# Revit family: Domotics-DomesticRanges-GEWISS-CHORUS_COMMAND-ONE-WAY_SWITCH_1M
name_source: partatom
category: Apparecchi elettrici
revit_build: Autodesk Revit 2016 (Build: 20161004_0715(x64)
units: mm (PartAtom-declared; Revit-internal decimal feet)

## family parameters
Condiviso = Sì
Host = Superficie
Mantenere orientamento annotazione = Sì
Numero OmniClass = 23.80.50.11.14
Punto di calcolo locali = Sì
Quota connettore circolare = Usa diametro
Taglio con vuoti quando caricato = Sì
Tipo di parte = Normale
Titolo OmniClass = Switches

## types (18) — shared parameters
Bidimensionale = bidimensionale interruttori 1m : GW12007
Breaking capacity: = 1.25 In (200 position changes)
Carico apparente = 0 VA
Catalogue = DOMOTICS
Catalogue Range = CHORUS - DOMESTIC RANGE
GW - Codice Electrocod = 0130
Glow Wire Test = 850°C
IDF = efd75715-110f-4a9d-a7a2-b49887324154
IDT = e4d6e52d-1028-4231-8f91-f4d5505fef12
Immagine tipo = GW14007.jpg
Insulation resistance = > 5 MOhm
Larghezza pulsante = 23 mm  [stored 0.0754593 ft]
N. poli = 1
No. Chorus modules = 1
Produttore = GEWISS S.p.A.
Prolonged operation (no.of position changes) = 40.000 at In 250 V ac cosÃ˜=0,6
Prospetto di default = 1219 mm
Resistance at test voltage = 2000 V at 50 Hz for 1 minute
SEO = 1 way switch
Simbolo_ = SIMBOLO INTERRUTTORI : INT2P
Standard; = EN 60669-1
Technical sheet = https://www.gewiss.com
Terminal grip on cable traction = > 50 N
Terminal tightening capacity flexible cables (mm2) = min. 0,75 - max. 2x4
Terminal tightening capacity rigid cables (mm2) = min. 0,5 - max. 2x2,5
Thermo-pressure with ball = 125
Tipo_ = CHORUS INTERRUTTORI 1M_BASE : GW14007 - Titanio
URL = https://www.gewiss.com
Version file RFA = 19.0
Volt = 230 V
Voltage = 250 V ac
Voltage: = 250 V ac
Wiring terminals = With screw

## per-type parameters (varying)
| type | Button key | Category | Colore | Description: | Descrizione | EAN code | GW - N. poli | Modello | Type | Type of use: |
| GW14002 - 1P - Titanium - Illuminable | With diffuser | One-way switch | Titanium | 1P - 16AX illuminable | 1-WAY SWITCH 1M 1P 16AX ILL LOC TITANIUM | 8011564265325 | 1P | GW14002 | Backlit |  |
| GW12002 - 1P - Black - Illuminable | With diffuser | One-way switch | Black | 1P - 16AX illuminable | 1-WAY SWITCH, 1M 1P 16AX ILL LOC BLACK | 8011564265240 | 1P | GW12002 | Backlit |  |
| GW10007 - 2P - White - heavy duty | Neutral | One-way switch | White | 2P - 25 AX | 1-WAY SWITCH 1M 2P 25AX HEAVY DUTY WHITE | 8011564260092 | 2P | GW10007 | Heavy duty | Heavy duty |
| GW14003 - 1P - Titanium - Illuminable | With replaceable neutral lens | One-way switch | Titanium | 1P - 16AX illuminable | 1-WAY SWITCH 1M 1P 16AX ILL SIG TITANIUM | 8011564265332 | 1P | GW14003 | Indicator |  |
| GW14005 - 2P - Titanium - Illuminable | With replaceable neutral lens | One-way switch | Titanium | 2P - 16AX illuminable | 1-WAY SWITCH 1M 2P 16AX ILL SIG TITANIUM | 8011564265356 | 2P | GW14005 | Indicator |  |
| GW10001 - 1P - White | Neutral | Switch | White | 1P - 16AX | 1-WAY SWITCH, 1M 1P 16AX WHITE | 8011564257825 | 1P | GW10001 | General |  |
| GW14004 - 2P - Titanium | Neutral | One-way switch | Titanium | 2P - 16 AX | 1-WAY SWITCH, 1M 2P 16AX TITANIUM | 8011564265349 | 2P | GW14004 | General |  |
| GW12007 - 2P - Black - heavy duty | Neutral | One-way switch | Black | 2P - 25 AX | 1-WAY SWITCH 1M 2P 25AX HEAVY DUTY BLACK | 8011564265295 | 2P | GW12007 | Heavy duty | Heavy duty |
| GW10002 - 1P - White - Illuminable | With diffuser | One-way switch | White | 1P - 16AX illuminable | 1-WAY SWITCH, 1M 1P 16AX ILL LOC WHITE | 8011564258167 | 1P | GW10002 | Backlit |  |
| GW12004 - 2P - Black | Neutral | One-way switch | Black | 2P - 16 AX | 1-WAY SWITCH, 1M 2P 16AX BLACK | 8011564265264 | 2P | GW12004 | General |  |
| GW10003 - 1P - White - Illuminable | With replaceable neutral lens | One-way switch | White | 1P - 16AX illuminable | 1-WAY SWITCH, 1M 1P 16AX ILL SIG WHITE | 8011564258174 | 1P | GW10003 | Indicator |  |
| GW10005 - 2P - White - Illuminable | With replaceable neutral lens | One-way switch | White | 2P - 16AX illuminable | 1-WAY SWITCH, 1M 2P 16AX ILL SIG WHITE | 8011564258198 | 2P | GW10005 | Indicator |  |
| GW10004 - 2P - White | Neutral | One-way switch | White | 2P - 16 AX | 1-WAY SWITCH, 1M 2P 16AX WHITE | 8011564258181 | 2P | GW10004 | General |  |
| GW14007 - 2P - Titanium - heavy duty | Neutral | One-way switch | Titanium | 2P - 25 AX | 1-WAY SW. 1M 2P 25AX HEAVY DUTY TITANIUM | 8011564265370 | 2P | GW14007 | Heavy duty | Heavy duty |
| GW12003 - 1P - Black - Illuminable | With replaceable neutral lens | One-way switch | Black | 1P - 16AX illuminable | 1-WAY SWITCH, 1M 1P 16AX ILL SIG BLACK | 8011564265257 | 1P | GW12003 | Indicator |  |
| GW12001 - 1P - Black | Neutral | One-way switch | Black | 1P - 16AX | 1-WAY SWITCH, 1M 1P 16AX BLACK | 8011564265233 | 1P | GW12001 | General |  |
| GW14001 - 1P - Titanium | Neutral | One-way switch | Titanium | 1P - 16AX | 1-WAY SWITCH, 1M 1P 16AX TITANIUM | 8011564265318 | 1P | GW14001 | General |  |
| GW12005 - 2P - Black - Illuminable | With replaceable neutral lens | One-way switch | Black | 2P - 16AX illuminable | 1-WAY SWITCH, 1M 2P 16AX ILL SIG BLACK | 8011564265271 | 2P | GW12005 | Indicator |  |

note: source unit labels omitted for Thermo-pressure with ball — the stored unit's dimension contradicts the parameter name (converter mislabeling)

note: [stored X ft] marks values corroborated as IEEE doubles in the binary element streams (Revit-internal decimal feet)

## geometry (parser evidence)
native form markers: Sweep x3
no freeform markers — native parametric forms only
